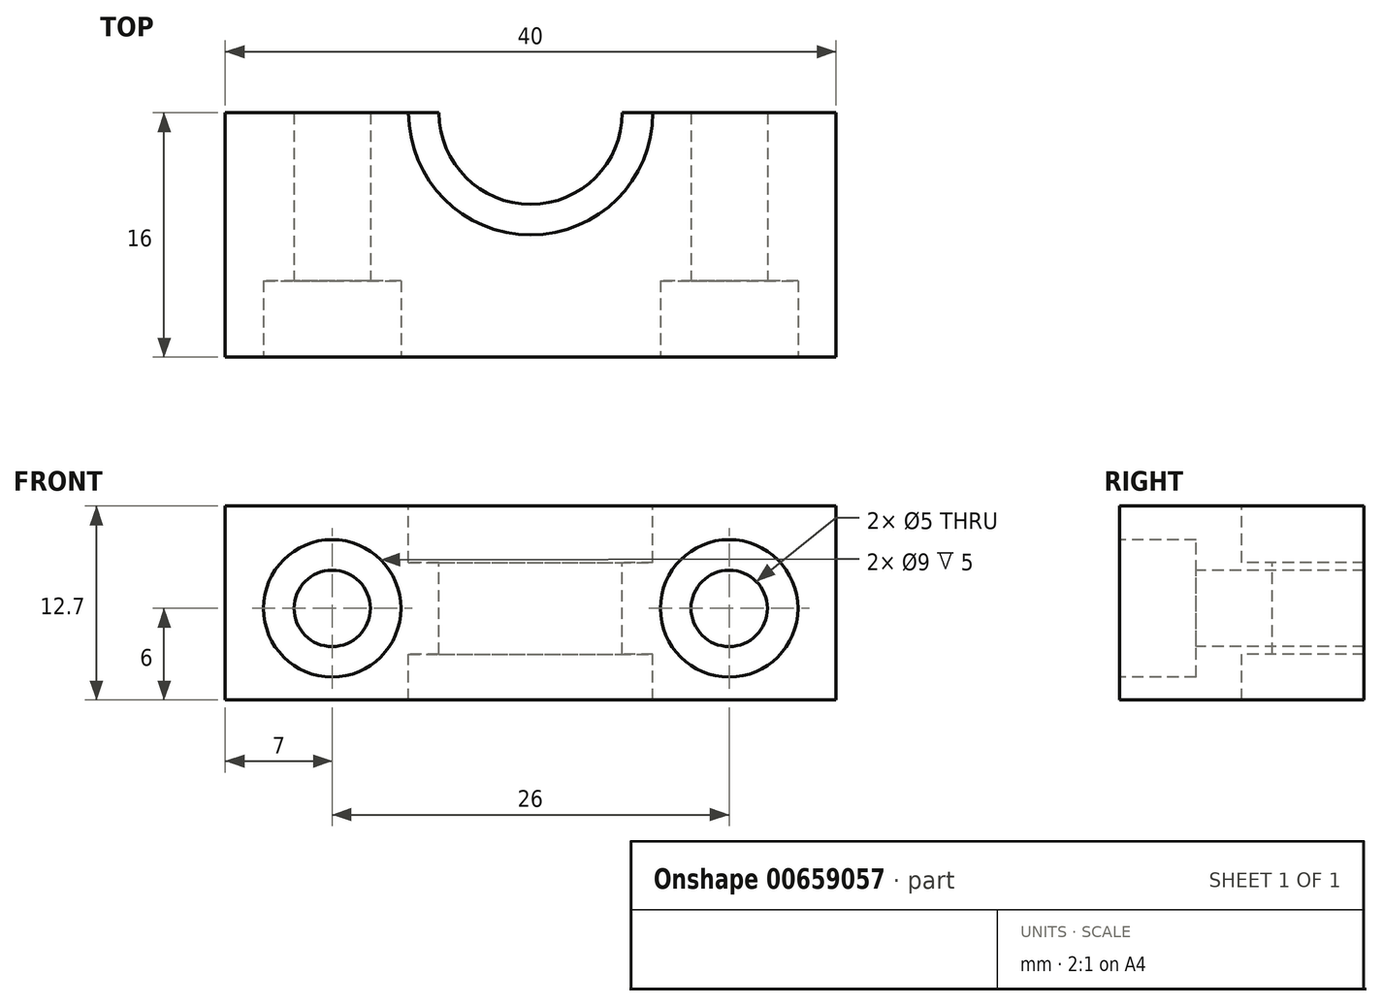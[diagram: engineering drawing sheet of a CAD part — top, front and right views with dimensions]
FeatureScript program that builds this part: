
annotation { "Feature Type Name" : "Feature", "Feature Type Description" : "" }
export const myFeature = defineFeature(function(context is Context, id is Id, definition is map)
    precondition{}
    {
        {
            var Q0;
            Q0=qCreatedBy(makeId("Top.planeOp"),FACE);
            var sketch = newSketch(context, id + "F0", { "sketchPlane" : qUnion([Q0])});
            skLineSegment(sketch, "E0.bottom", {"start": v(20, 8) * mm, "end": v(-20, 8) * mm});
            skLineSegment(sketch, "E0.top", {"start": v(20, -8) * mm, "end": v(-20, -8) * mm});
            skLineSegment(sketch, "E0.left", {"start": v(20, 8) * mm, "end": v(20, -8) * mm});
            skLineSegment(sketch, "E0.right", {"start": v(-20, 8) * mm, "end": v(-20, -8) * mm});
            skPoint(sketch, "E0.middle", {"position": v(0, 0) * mm});
            skSolve(sketch);
        }
        {
            var Q0;
            Q0=makeQuery(id+"F0.imprint","IMPRINT",FACE,{"disambiguationData":[TD([[makeQuery(id+"F0.imprint","IMPRINT",EDGE,{"derivedFrom":sQuery(id+"F0.wireOp",EDGE,"E0.bottom")}),1.0]])]});
            extrude(context, id + "F1", {"entities" : qUnion([Q0]), "depth" : 12.7 * mm, "offsetDistance" : 25 * mm});
        }
        {
            var Q0;
            Q0=makeQuery(id+"F1.opExtrude","CAP_FACE",FACE,{"disambiguationData":[OSD([sQuery(id+"F0.wireOp",EDGE,"E0.bottom"),sQuery(id+"F0.wireOp",EDGE,"E0.top"),sQuery(id+"F0.wireOp",EDGE,"E0.left"),sQuery(id+"F0.wireOp",EDGE,"E0.right")])],"isStart":false});
            var sketch = newSketch(context, id + "F2", { "sketchPlane" : qUnion([Q0])});
            skCircle(sketch, "E1", {"center": v(0, 8) * mm, "radius": 8 * mm});
            skSolve(sketch);
        }
        {
            var Q0;
            {var subQ0=sQuery(id+"F2.wireOp",EDGE,"E1");var subQ1=makeQuery(id+"F1.opExtrude","CAP_EDGE",EDGE,{"disambiguationData":[OSD([sQuery(id+"F0.wireOp",EDGE,"E0.bottom")])],"isStart":false});var subQ2=makeQuery(id+"F2.imprint","INTERSECT",VERTEX,{"disambiguationData":[OD(0.0)],"derivedFrom":[subQ1,subQ0]});Q0=makeQuery(id+"F2.imprint","IMPRINT",FACE,{"disambiguationData":[TD([[makeQuery(id+"F2.imprint","IMPRINT",EDGE,{"disambiguationData":[TD([[subQ2,1.0]])],"derivedFrom":subQ0}),1.0]])]});}
            extrude(context, id + "F3", {"entities" : qUnion([Q0]), "operationType" : NewBodyOperationType.REMOVE, "oppositeDirection" : true, "depth" : 3.7 * mm, "offsetDistance" : 25 * mm});
        }
        {
            var Q0;
            Q0=makeQuery(id+"F3.boolean.opBoolean","COPY",FACE,{"derivedFrom":makeQuery(id+"F3.opExtrude","CAP_FACE",FACE,{"disambiguationData":[OSD([sQuery(id+"F0.wireOp",EDGE,"E0.bottom"),sQuery(id+"F2.wireOp",EDGE,"E1")])],"isStart":false})});
            var sketch = newSketch(context, id + "F4", { "sketchPlane" : qUnion([Q0])});
            skCircle(sketch, "E2", {"center": v(0, 8) * mm, "radius": 6 * mm});
            skSolve(sketch);
        }
        {
            var Q0;
            Q0 = qSketchRegion(id + "F4", true);
            extrude(context, id + "F5", {"entities" : qUnion([Q0]), "operationType" : NewBodyOperationType.REMOVE, "oppositeDirection" : true, "depth" : 6 * mm, "offsetDistance" : 25 * mm});
        }
        {
            var Q0;
            Q0=makeQuery(id+"F5.boolean.opBoolean","COPY",FACE,{"derivedFrom":makeQuery(id+"F5.opExtrude","CAP_FACE",FACE,{"disambiguationData":[OSD([sQuery(id+"F4.wireOp",EDGE,"E2")])],"isStart":false})});
            var sketch = newSketch(context, id + "F6", { "sketchPlane" : qUnion([Q0])});
            skCircle(sketch, "E3", {"center": v(0, 8) * mm, "radius": 8 * mm});
            skSolve(sketch);
        }
        {
            var Q0;
            Q0 = qSketchRegion(id + "F6", true);
            extrude(context, id + "F7", {"entities" : qUnion([Q0]), "operationType" : NewBodyOperationType.REMOVE, "oppositeDirection" : true, "depth" : 3 * mm, "offsetDistance" : 25 * mm});
        }
        {
            var Q0;
            Q0=makeQuery(id+"F1.opExtrude","SWEPT_FACE",FACE,{"disambiguationData":[OSD([sQuery(id+"F0.wireOp",EDGE,"E0.top")])]});
            var sketch = newSketch(context, id + "F8", { "sketchPlane" : qUnion([Q0])});
            skPoint(sketch, "E4", {"position": v(0, 6) * mm});
            skPoint(sketch, "E5", {"position": v(13, 6) * mm});
            skPoint(sketch, "E6", {"position": v(-13, 6) * mm});
            skSolve(sketch);
        }
        {
            var Q0;
            Q0=sQuery(id+"F8.wireOp",VERTEX,"E6");
            var Q1;
            Q1=sQuery(id+"F8.wireOp",VERTEX,"E5");
            var Q2;
            Q2=makeQuery(id+"F1.opExtrude","SWEPT_BODY",BODY,{"disambiguationData":[OSD([sQuery(id+"F0.wireOp",EDGE,"E0.bottom"),sQuery(id+"F0.wireOp",EDGE,"E0.top"),sQuery(id+"F0.wireOp",EDGE,"E0.left"),sQuery(id+"F0.wireOp",EDGE,"E0.right")])]});
            hole(context, id + "F9", {"style" : HoleStyle.C_BORE, "endStyle" : HoleEndStyle.THROUGH, "holeDiameter" : 5 * mm, "cBoreDiameter" : 9 * mm, "cBoreDepth" : 5 * mm, "majorDiameter" : 5 * mm, "isTappedThrough" : true, "tappedDepth" : 12 * mm, "tapClearance" : 3, "locations" : qUnion([Q0, Q1]), "scope" : qUnion([Q2])});
        }
    });
